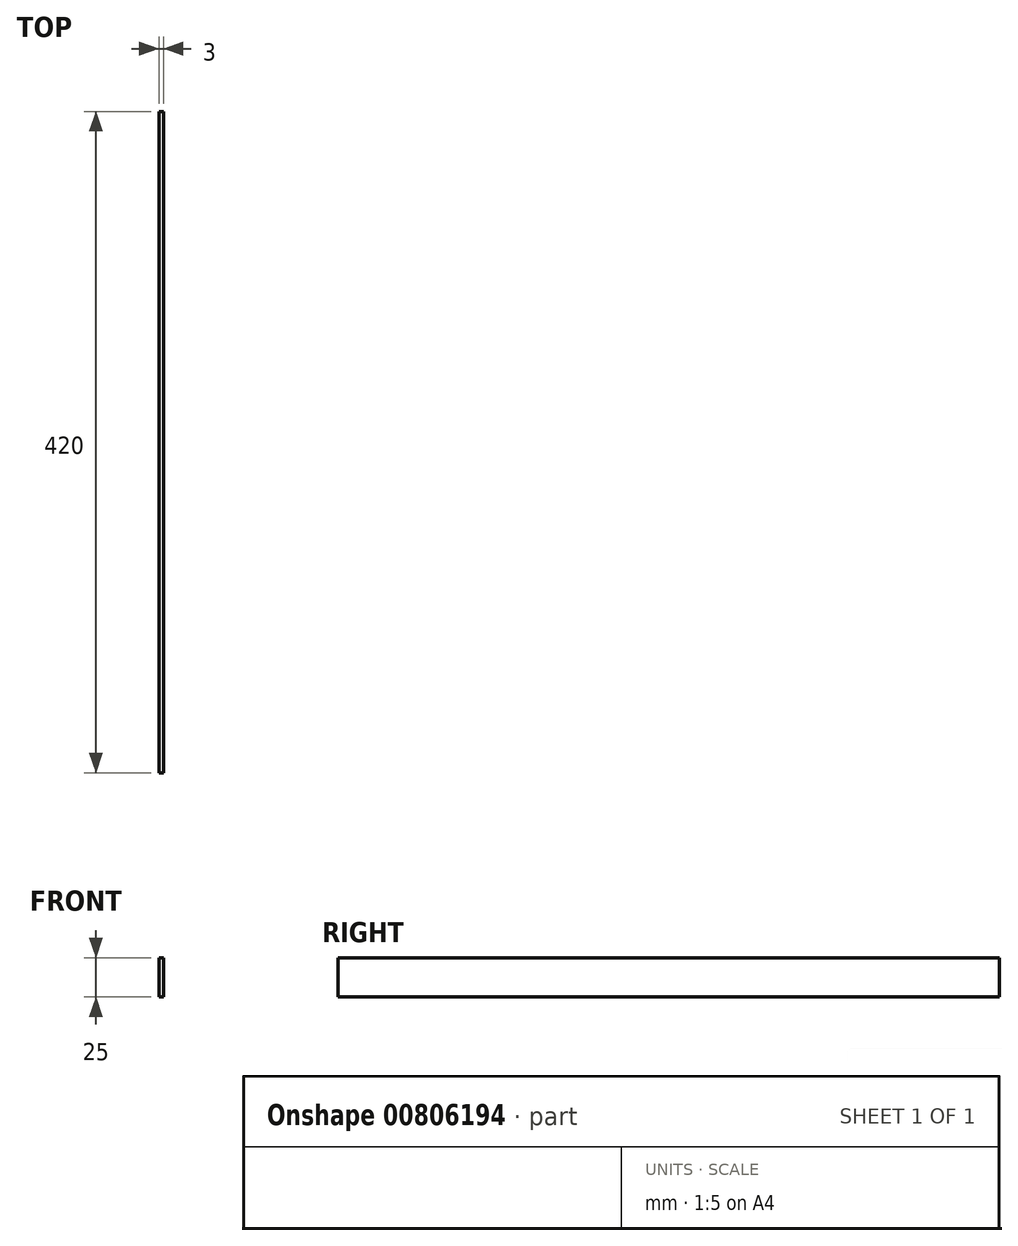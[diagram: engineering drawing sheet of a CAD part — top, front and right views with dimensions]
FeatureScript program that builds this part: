
annotation { "Feature Type Name" : "Feature", "Feature Type Description" : "" }
export const myFeature = defineFeature(function(context is Context, id is Id, definition is map)
    precondition{}
    {
        {
            var Q0;
            Q0=qCreatedBy(makeId("Front.planeOp"),FACE);
            var sketch = newSketch(context, id + "F0", { "sketchPlane" : qUnion([Q0])});
            skLineSegment(sketch, "E0.bottom", {"start": v(1.5, -12.5) * mm, "end": v(-1.5, -12.5) * mm});
            skLineSegment(sketch, "E0.top", {"start": v(1.5, 12.5) * mm, "end": v(-1.5, 12.5) * mm});
            skLineSegment(sketch, "E0.left", {"start": v(1.5, -12.5) * mm, "end": v(1.5, 12.5) * mm});
            skLineSegment(sketch, "E0.right", {"start": v(-1.5, -12.5) * mm, "end": v(-1.5, 12.5) * mm});
            skPoint(sketch, "E0.middle", {"position": v(0, 0) * mm});
            skSolve(sketch);
        }
        {
            var Q0;
            Q0=qSketchRegion(id+"F0",true);
            extrude(context, id + "F1", {"entities" : qUnion([Q0]), "depth" : 420 * mm, "offsetDistance" : 25 * mm});
        }
    });
